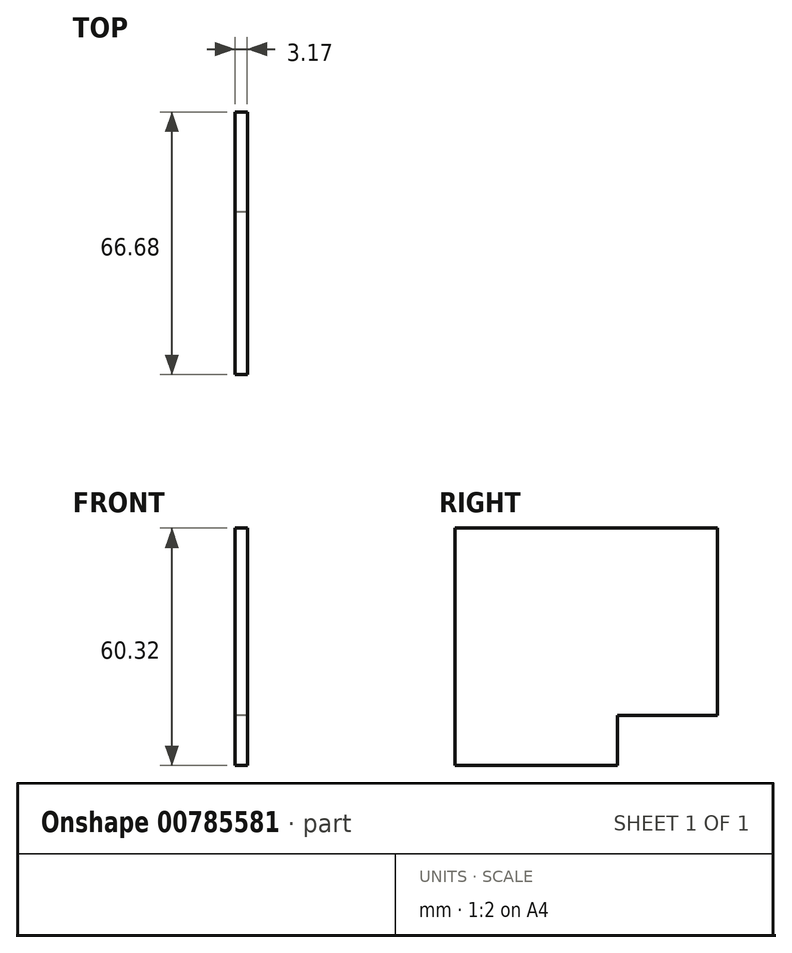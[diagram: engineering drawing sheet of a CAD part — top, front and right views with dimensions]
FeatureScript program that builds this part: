
annotation { "Feature Type Name" : "Feature", "Feature Type Description" : "" }
export const myFeature = defineFeature(function(context is Context, id is Id, definition is map)
    precondition{}
    {
        {
            var Q0;
            Q0=qCreatedBy(makeId("Right.planeOp"),FACE);
            var sketch = newSketch(context, id + "F0", { "sketchPlane" : qUnion([Q0])});
            skLineSegment(sketch, "E0.bottom", {"start": v(-33.34, 30.16) * mm, "end": v(33.34, 30.16) * mm});
            skLineSegment(sketch, "E0.top", {"start": v(-33.34, -30.16) * mm, "end": v(33.34, -30.16) * mm});
            skLineSegment(sketch, "E0.left", {"start": v(-33.34, 30.16) * mm, "end": v(-33.34, -30.16) * mm});
            skLineSegment(sketch, "E0.right", {"start": v(33.34, 30.16) * mm, "end": v(33.34, -30.16) * mm});
            skPoint(sketch, "E0.middle", {"position": v(0, 0) * mm});
            skLineSegment(sketch, "E1.bottom", {"start": v(33.34, -30.16) * mm, "end": v(7.94, -30.16) * mm});
            skLineSegment(sketch, "E1.top", {"start": v(33.34, -17.46) * mm, "end": v(7.94, -17.46) * mm});
            skLineSegment(sketch, "E1.left", {"start": v(33.34, -30.16) * mm, "end": v(33.34, -17.46) * mm});
            skLineSegment(sketch, "E1.right", {"start": v(7.94, -30.16) * mm, "end": v(7.94, -17.46) * mm});
            skSolve(sketch);
        }
        {
            var Q0;
            {var subQ1=sQuery(id+"F0.wireOp",EDGE,"E0.bottom");Q0=makeQuery(id+"F0.imprint","IMPRINT",FACE,{"disambiguationData":[TD([[makeQuery(id+"F0.imprint","IMPRINT",EDGE,{"derivedFrom":subQ1}),-1.0]])]});}
            extrude(context, id + "F1", {"entities" : qUnion([Q0]), "depth" : 3.17 * mm, "offsetDistance" : 25.4 * mm});
        }
    });
